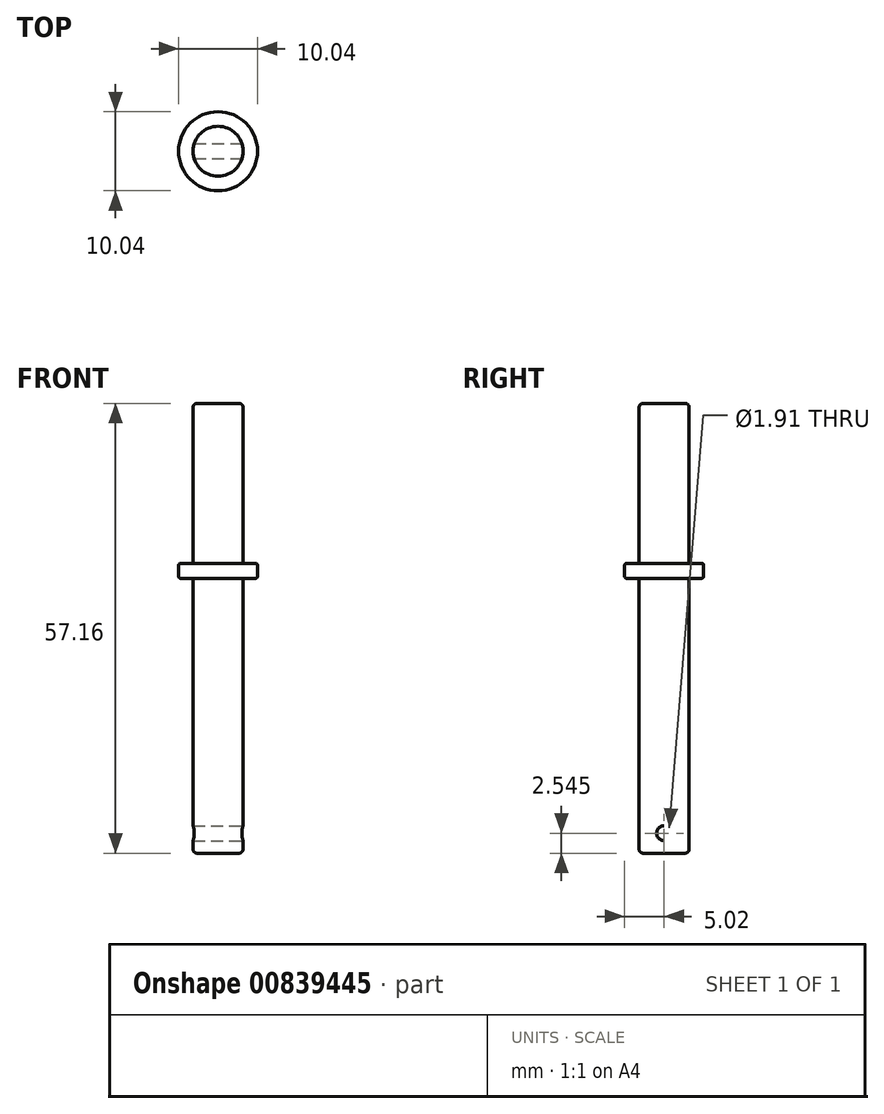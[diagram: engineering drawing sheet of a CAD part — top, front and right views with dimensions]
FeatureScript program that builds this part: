
annotation { "Feature Type Name" : "Feature", "Feature Type Description" : "" }
export const myFeature = defineFeature(function(context is Context, id is Id, definition is map)
    precondition{}
    {
        {
            var Q0;
            Q0=qCreatedBy(makeId("Top.planeOp"),FACE);
            var sketch = newSketch(context, id + "F0", { "sketchPlane" : qUnion([Q0])});
            skCircle(sketch, "E0", {"center": v(0, 0) * mm, "radius": 3.18 * mm});
            skSolve(sketch);
        }
        {
            var Q0;
            Q0=qSketchRegion(id+"F0",true);
            extrude(context, id + "F1", {"entities" : qUnion([Q0]), "depth" : 57.15 * mm, "offsetDistance" : 25.4 * mm, "symmetric" : true});
        }
        {
            var Q0;
            Q0=makeQuery(id+"F1.opExtrude","CAP_FACE",FACE,{"disambiguationData":[OSD([sQuery(id+"F0.wireOp",EDGE,"E0")])],"isStart":false});
            cPlane(context, id + "F2", {"entities" : qUnion([Q0]), "cplaneType" : CPlaneType.OFFSET, "offset" : 22.22 * mm, "oppositeDirection" : true, "width" : 152.4 * mm, "height" : 152.4 * mm});
        }
        {
            var Q0;
            Q0=qCreatedBy(id+"F2.planeOp",FACE);
            var sketch = newSketch(context, id + "F3", { "sketchPlane" : qUnion([Q0])});
            skCircle(sketch, "E1", {"center": v(0, 0) * mm, "radius": 5.02 * mm});
            skSolve(sketch);
        }
        {
            var Q0;
            Q0=qSketchRegion(id+"F3",true);
            extrude(context, id + "F4", {"entities" : qUnion([Q0]), "operationType" : NewBodyOperationType.ADD, "depth" : 1.9 * mm, "offsetDistance" : 25.4 * mm});
        }
        {
            var Q0;
            Q0=makeQuery(id+"F4.opExtrude","CAP_EDGE",EDGE,{"disambiguationData":[OSD([sQuery(id+"F3.wireOp",EDGE,"E1")])],"isStart":false});
            var Q1;
            Q1=makeQuery(id+"F4.opExtrude","CAP_EDGE",EDGE,{"disambiguationData":[OSD([sQuery(id+"F3.wireOp",EDGE,"E1")])],"isStart":true});
            fillet(context, id + "F5", {"entities" : qUnion([Q0, Q1]), "tangentPropagation" : true, "radius" : 0.25 * mm, "defaultsChanged" : false, "vertexSettings" : [], "allowEdgeOverflow" : false});
        }
        {
            var Q0;
            Q0=qCreatedBy(makeId("Right.planeOp"),FACE);
            var sketch = newSketch(context, id + "F6", { "sketchPlane" : qUnion([Q0])});
            skCircle(sketch, "E2", {"center": v(0, -26.04) * mm, "radius": 0.95 * mm});
            skSolve(sketch);
        }
        {
            var Q0;
            Q0 = qSketchRegion(id + "F6", true);
            extrude(context, id + "F7", {"entities" : qUnion([Q0]), "operationType" : NewBodyOperationType.REMOVE, "endBound" : BoundingType.THROUGH_ALL, "oppositeDirection" : true, "depth" : 25.4 * mm, "offsetDistance" : 25.4 * mm, "hasSecondDirection" : true, "secondDirectionOppositeDirection" : false, "secondDirectionDepth" : 25.4 * mm});
        }
        {
            var Q0;
            Q0=makeQuery(id+"F1.opExtrude","CAP_EDGE",EDGE,{"disambiguationData":[OSD([sQuery(id+"F0.wireOp",EDGE,"E0")])],"isStart":false});
            var Q1;
            Q1=makeQuery(id+"F1.opExtrude","CAP_EDGE",EDGE,{"disambiguationData":[OSD([sQuery(id+"F0.wireOp",EDGE,"E0")])],"isStart":true});
            fillet(context, id + "F8", {"entities" : qUnion([Q0, Q1]), "tangentPropagation" : true, "radius" : 0.5 * mm, "defaultsChanged" : false, "vertexSettings" : [], "allowEdgeOverflow" : false});
        }
    });
